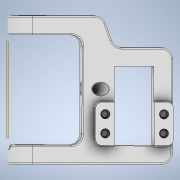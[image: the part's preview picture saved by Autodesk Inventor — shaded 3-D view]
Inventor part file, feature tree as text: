
AUTODESK INVENTOR PART (.ipt)
format: ipt  version: 2020.3 (Build 243373000, 373)  size: 531,968 bytes
history: native  units: mm
features: fillet x11, sketch x8, extrude x6, hole x5, plane x2, chamfer x1
ambient origin geometry x8: Origin, YZ Plane, XZ Plane, XY Plane, X Axis, Y Axis, Z Axis, Center Point
bodies: Solid1 (feature_tree)
feature tree (33):
  sketch  "Sketch1"  dims[d4=24.6mm d5=12.4mm]
  extrude  "Extrusion1"  Depth=12.4mm
  hole  "Hole1"  [1 undecoded]
  fillet  "Fillet1"  Radius=23.0mm
  fillet  "Fillet2"  Radius=34.5mm
  sketch  "Sketch2"  dims[d9=6.0mm d11=10.0mm d12=23.0mm d14=34.5mm]
  hole  "Hole2"  [1 undecoded]
  sketch  "Sketch8"  dims[d19=1.9mm d20=6.0mm d21=4.0mm d22=2.0mm d23=90.0deg d24=10.0mm d25=20.594885mm]
  extrude  "Extrusion3"  Depth=6.0mm
  extrude  "Extrusion4"  Depth=3.7mm
  hole  "Hole5"  [1 undecoded]
  fillet  "Fillet4"  Radius=10.0mm
  fillet  "Fillet9"  Radius=3.5mm
  fillet  "Fillet10"  Radius=0.5mm
  fillet  "Fillet5"  Radius=0.5mm
  fillet  "Fillet6"  Radius=28.4mm
  hole  "Hole4"  [1 undecoded]
  fillet  "Fillet11"  Radius=6.0mm
  extrude  "Extrusion6"  Depth=2.0mm
  plane  "Work Plane1"
  extrude  "Extrusion7"  Depth=0.5mm
  fillet  "Fillet12"  Radius=2.0mm
  hole  "Hole6"  [1 undecoded]
  plane  "Work Plane3"
  extrude  "Extrusion8"  Depth=2.0mm
  chamfer  "Chamfer1"  Distance=0.3mm
  fillet  "Fillet13"  Radius=0.2mm
  fillet  "Fillet14"  [1 undecoded]
  sketch  "Sketch3"  dims[d16=6.0mm d17=15.0mm d18=0.0mm]
  sketch  "Sketch9"  dims[d27=8.8mm d28=6.0mm d29=4.0mm d30=2.0mm d31=90.0deg d32=8.0mm d33=20.594885mm d34=6.0mm]
  sketch  "Sketch10"  dims[d37=7.2mm d38=3.7mm]
  sketch  "Sketch11"  dims[d39=12.1mm d40=3.5mm d41=0.0mm d42=10.0mm d43=0.0mm d53=3.5mm d54=0.5mm d55=0.5mm d57=28.4mm]
  sketch  "Sketch12"  dims[d58=6.8mm d59=20.92mm d60=0.0mm d61=6.0mm d62=3.0mm d63=6.0mm d64=4.0mm d65=2.0mm d66=90.0deg d67=4.3mm d68=0.0mm d70=2.0mm d71=0.5mm d72=2.0mm d74=2.0mm d75=2.0mm d76=1.0mm d77=6.0mm d78=4.0mm d79=2.0mm d80=90.0deg d81=8.0mm d82=20.594885mm d83=0.3mm d84=0.2mm d85=0.0mm d86=0.0mm d87=1.0mm d88=3.5mm d89=-9.075712mm d90=4.0mm d91=4.0mm d92=1.0mm d93=33.941mm d94=0.0mm d95=0.2mm d96=2.1mm d97=6.0mm d98=4.0mm d99=2.0mm d100=90.0deg d101=7.3mm d102=0.0mm d103=23.0mm d104=7.0mm d105=7.0mm d106=0.0mm d107=0.2mm d108=0.8mm d109=45.0deg d110=1.0mm d111=2.0mm d112=3.490659mm]
note: 6 required parameter values undecoded (feature->parameter linkage not recoverable at this tier; creation-order binding heuristic only, values carry confidence <= 0.55)
